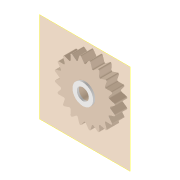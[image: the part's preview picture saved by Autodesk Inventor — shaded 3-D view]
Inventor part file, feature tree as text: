
AUTODESK INVENTOR PART (.ipt)
format: ipt  version: 2022 (Build 260153000, 153)  size: 172,032 bytes
history: native  units: mm
features: extrude x3, sketch x3, plane x1, fillet x1, pattern_circular x1
ambient origin geometry x8: Origin, YZ Plane, XZ Plane, XY Plane, X Axis, Y Axis, Z Axis, Center Point
bodies: Volumenkörper1 (feature_tree)
feature tree (9):
  extrude  "Extrusion1"  Depth=15.0mm
  plane  "Arbeitsebene1"
  extrude  "Extrusion2"  Depth=3.0mm TaperAngle=0.0deg
  extrude  "Extrusion4"  Depth=0.5mm TaperAngle=0.0deg
  fillet  "Rundung2"  Radius=9.599311mm
  pattern_circular  "Runde Anordnung3"  [2 undecoded]
  sketch  "Skizze1"  dims[d0=2.9mm d1=15.0mm]
  sketch  "Skizze2"  dims[d2=3.0mm d3=0.0mm d6=5.0mm d7=0.0mm]
  sketch  "Skizze5"  dims[d14=5.0mm d15=0.5mm d16=0.0mm d17=9.599311mm d18=21.816616mm d22=0.25mm d23=200.0mm d24=360.0deg]
note: 2 required parameter values undecoded (feature->parameter linkage not recoverable at this tier; creation-order binding heuristic only, values carry confidence <= 0.55)
